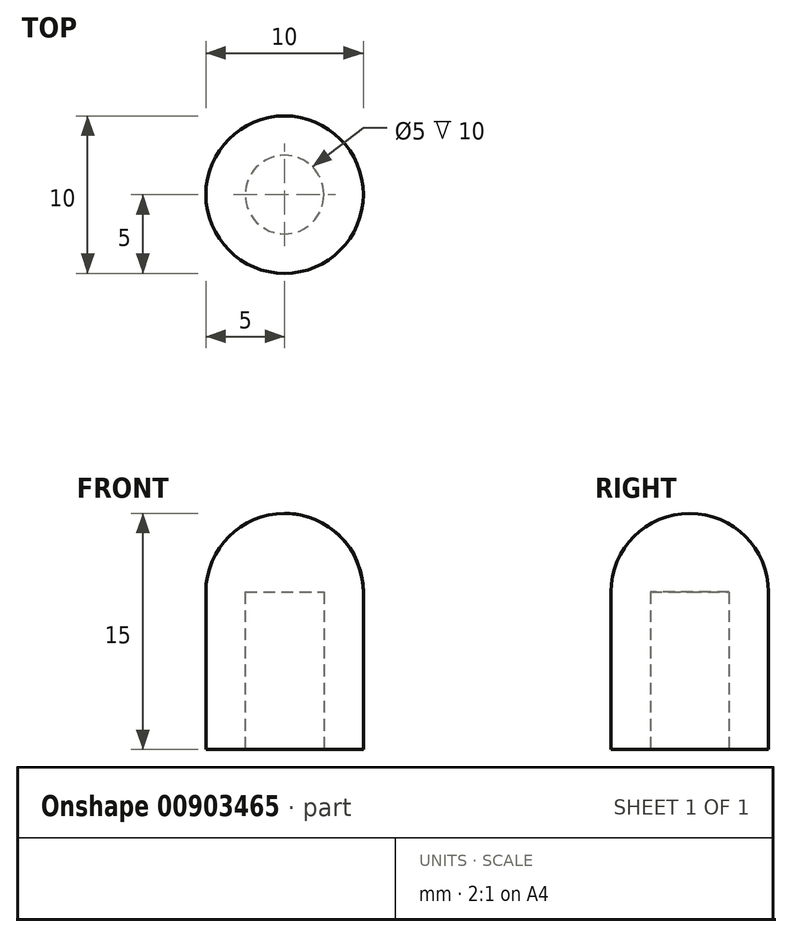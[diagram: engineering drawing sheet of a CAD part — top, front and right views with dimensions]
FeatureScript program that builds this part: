
annotation { "Feature Type Name" : "Feature", "Feature Type Description" : "" }
export const myFeature = defineFeature(function(context is Context, id is Id, definition is map)
    precondition{}
    {
        {
            var Q0;
            Q0=qCreatedBy(makeId("Front.planeOp"),FACE);
            var sketch = newSketch(context, id + "F0", { "sketchPlane" : qUnion([Q0])});
            skLineSegment(sketch, "E0", {"start": v(-5, 0) * mm, "end": v(-2.5, 0) * mm});
            skLineSegment(sketch, "E1", {"start": v(-2.5, 0) * mm, "end": v(-2.5, 10) * mm});
            skLineSegment(sketch, "E2", {"start": v(-5, 0) * mm, "end": v(-5, 10) * mm});
            skLineSegment(sketch, "E3", {"start": v(-2.5, 10) * mm, "end": v(0, 10) * mm});
            skLineSegment(sketch, "E4", {"start": v(0, 10) * mm, "end": v(0, 15) * mm});
            skArc(sketch, "E5", {"start": v(0, 15) * mm, "mid": v(-3.54, 13.54) * mm, "end": v(-5, 10) * mm});
            skSolve(sketch);
        }
        {
            var Q0;
            Q0=makeQuery(id+"F0.imprint","IMPRINT",FACE,{"disambiguationData":[TD([[makeQuery(id+"F0.imprint","IMPRINT",EDGE,{"derivedFrom":sQuery(id+"F0.wireOp",EDGE,"E0")}),1.0]])]});
            var Q1;
            Q1=sQuery(id+"F0.wireOp",EDGE,"E4");
            revolve(context, id + "F1", {"surfaceOperationType" : NewSurfaceOperationType.NEW, "entities" : qUnion([Q0]), "axis" : qUnion([Q1]), "revolveType" : RevolveType.FULL});
        }
    });
